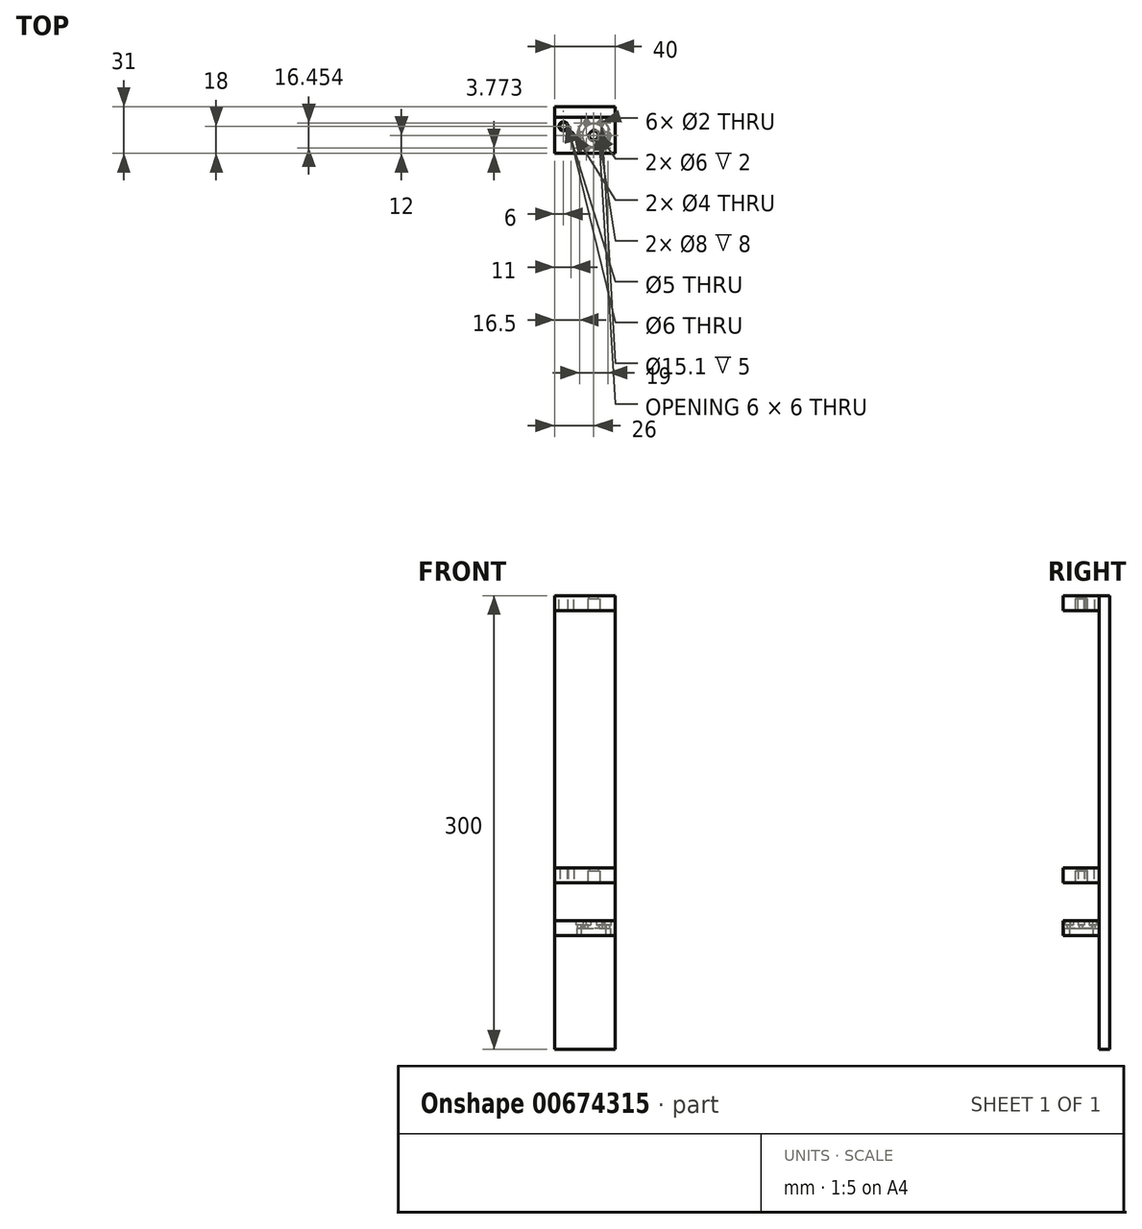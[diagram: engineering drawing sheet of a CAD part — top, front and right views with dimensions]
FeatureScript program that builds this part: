
annotation { "Feature Type Name" : "Feature", "Feature Type Description" : "" }
export const myFeature = defineFeature(function(context is Context, id is Id, definition is map)
    precondition{}
    {
        {
            var Q0;
            Q0=qCreatedBy(makeId("Top.planeOp"),FACE);
            var sketch = newSketch(context, id + "F0", { "sketchPlane" : qUnion([Q0])});
            skLineSegment(sketch, "E0.bottom", {"start": v(0, 0) * mm, "end": v(40, 0) * mm});
            skLineSegment(sketch, "E0.top", {"start": v(0, 24) * mm, "end": v(40, 24) * mm});
            skLineSegment(sketch, "E0.left", {"start": v(0, 0) * mm, "end": v(0, 24) * mm});
            skLineSegment(sketch, "E0.right", {"start": v(40, 0) * mm, "end": v(40, 24) * mm});
            skCircle(sketch, "E1", {"center": v(26, 12) * mm, "radius": 7.55 * mm});
            skLineSegment(sketch, "E2", {"start": v(0, 12) * mm, "end": v(40, 12) * mm, "construction": true});
            skSolve(sketch);
        }
        {
            var Q0;
            Q0 = qSketchRegion(id + "F0", true);
            extrude(context, id + "F1", {"entities" : qUnion([Q0]), "depth" : 10 * mm, "offsetDistance" : 25 * mm});
        }
        {
            var Q0;
            Q0=makeQuery(id+"F1.opExtrude","CAP_FACE",FACE,{"disambiguationData":[OSD([sQuery(id+"F0.wireOp",EDGE,"E0.bottom"),sQuery(id+"F0.wireOp",EDGE,"E0.top"),sQuery(id+"F0.wireOp",EDGE,"E0.left"),sQuery(id+"F0.wireOp",EDGE,"E0.right"),sQuery(id+"F0.wireOp",EDGE,"E1")])],"isStart":false});
            var sketch = newSketch(context, id + "F2", { "sketchPlane" : qUnion([Q0])});
            skCircle(sketch, "E3.cCircle", {"center": v(26, 12) * mm, "radius": 9.5 * mm, "construction": true});
            skLineSegment(sketch, "E3.0", {"start": v(21.25, 20.23) * mm, "end": v(30.75, 20.23) * mm, "construction": true});
            skLineSegment(sketch, "E3.1", {"start": v(30.75, 20.23) * mm, "end": v(35.5, 12) * mm, "construction": true});
            skLineSegment(sketch, "E3.2", {"start": v(35.5, 12) * mm, "end": v(30.75, 3.77) * mm, "construction": true});
            skLineSegment(sketch, "E3.3", {"start": v(30.75, 3.77) * mm, "end": v(21.25, 3.77) * mm, "construction": true});
            skLineSegment(sketch, "E3.4", {"start": v(21.25, 3.77) * mm, "end": v(16.5, 12) * mm, "construction": true});
            skLineSegment(sketch, "E3.5", {"start": v(16.5, 12) * mm, "end": v(21.25, 20.23) * mm, "construction": true});
            skLineSegment(sketch, "E4", {"start": v(21.25, 20.23) * mm, "end": v(30.75, 3.77) * mm, "construction": true});
            skPoint(sketch, "E5", {"position": v(21.25, 20.23) * mm});
            skPoint(sketch, "E6", {"position": v(16.5, 12) * mm});
            skPoint(sketch, "E7", {"position": v(21.25, 3.77) * mm});
            skPoint(sketch, "E8", {"position": v(30.75, 3.77) * mm});
            skPoint(sketch, "E9", {"position": v(35.5, 12) * mm});
            skPoint(sketch, "E10", {"position": v(30.75, 20.23) * mm});
            skSolve(sketch);
        }
        {
            var Q0;
            Q0=sQuery(id+"F2.wireOp",VERTEX,"E5");
            var Q1;
            Q1=sQuery(id+"F2.wireOp",VERTEX,"E6");
            var Q2;
            Q2=sQuery(id+"F2.wireOp",VERTEX,"E7");
            var Q3;
            Q3=sQuery(id+"F2.wireOp",VERTEX,"E8");
            var Q4;
            Q4=sQuery(id+"F2.wireOp",VERTEX,"E9");
            var Q5;
            Q5=sQuery(id+"F2.wireOp",VERTEX,"E10");
            var Q6;
            Q6=makeQuery(id+"F1.opExtrude","SWEPT_BODY",BODY,{"disambiguationData":[OSD([sQuery(id+"F0.wireOp",EDGE,"E0.bottom"),sQuery(id+"F0.wireOp",EDGE,"E0.top"),sQuery(id+"F0.wireOp",EDGE,"E0.left"),sQuery(id+"F0.wireOp",EDGE,"E0.right"),sQuery(id+"F0.wireOp",EDGE,"E1")])]});
            hole(context, id + "F3", {"style" : HoleStyle.SIMPLE, "endStyle" : HoleEndStyle.BLIND, "holeDiameter" : 2 * mm, "majorDiameter" : 5 * mm, "holeDepth" : 18 * mm, "isTappedThrough" : true, "tappedDepth" : 7 * mm, "tapClearance" : 2, "startFromSketch" : true, "locations" : qUnion([Q0, Q1, Q2, Q3, Q4, Q5]), "scope" : qUnion([Q6])});
        }
        {
            var Q0;
            Q0=makeQuery(id+"F1.opExtrude","CAP_FACE",FACE,{"disambiguationData":[OSD([sQuery(id+"F0.wireOp",EDGE,"E0.bottom"),sQuery(id+"F0.wireOp",EDGE,"E0.top"),sQuery(id+"F0.wireOp",EDGE,"E0.left"),sQuery(id+"F0.wireOp",EDGE,"E0.right"),sQuery(id+"F0.wireOp",EDGE,"E1")])],"isStart":false});
            var sketch = newSketch(context, id + "F4", { "sketchPlane" : qUnion([Q0])});
            skCircle(sketch, "E11", {"center": v(21.25, 20.23) * mm, "radius": 2 * mm});
            skCircle(sketch, "E12", {"center": v(30.75, 3.77) * mm, "radius": 2 * mm});
            skLineSegment(sketch, "E13", {"start": v(19.52, 19.23) * mm, "end": v(29.02, 2.77) * mm});
            skLineSegment(sketch, "E14", {"start": v(22.98, 21.23) * mm, "end": v(32.48, 4.77) * mm});
            skLineSegment(sketch, "E15.1.0", {"start": v(22.98, 2.77) * mm, "end": v(32.48, 19.23) * mm});
            skCircle(sketch, "E15.1.1", {"center": v(21.25, 3.77) * mm, "radius": 2 * mm});
            skLineSegment(sketch, "E15.1.2", {"start": v(19.52, 4.77) * mm, "end": v(29.02, 21.23) * mm});
            skCircle(sketch, "E15.1.3", {"center": v(30.75, 20.23) * mm, "radius": 2 * mm});
            skLineSegment(sketch, "E15.2.0", {"start": v(35.5, 14) * mm, "end": v(16.5, 14) * mm});
            skCircle(sketch, "E15.2.1", {"center": v(35.5, 12) * mm, "radius": 2 * mm});
            skLineSegment(sketch, "E15.2.2", {"start": v(35.5, 10) * mm, "end": v(16.5, 10) * mm});
            skCircle(sketch, "E15.2.3", {"center": v(16.5, 12) * mm, "radius": 2 * mm});
            skPoint(sketch, "E15.center", {"position": v(26, 12) * mm});
            skSolve(sketch);
        }
        {
            var Q0;
            Q0 = qSketchRegion(id + "F4", true);
            extrude(context, id + "F5", {"entities" : qUnion([Q0]), "operationType" : NewBodyOperationType.REMOVE, "oppositeDirection" : true, "depth" : 3 * mm, "offsetDistance" : 25 * mm});
        }
        {
            var Q0;
            Q0=makeQuery(id+"F1.opExtrude","CAP_FACE",FACE,{"disambiguationData":[OSD([sQuery(id+"F0.wireOp",EDGE,"E0.bottom"),sQuery(id+"F0.wireOp",EDGE,"E0.top"),sQuery(id+"F0.wireOp",EDGE,"E0.left"),sQuery(id+"F0.wireOp",EDGE,"E0.right"),sQuery(id+"F0.wireOp",EDGE,"E1")])],"isStart":true});
            var sketch = newSketch(context, id + "F6", { "sketchPlane" : qUnion([Q0])});
            skCircle(sketch, "E16", {"center": v(26, -12) * mm, "radius": 11.1 * mm});
            skLineSegment(sketch, "E17.bottom", {"start": v(18, -0.65) * mm, "end": v(34, -0.65) * mm});
            skLineSegment(sketch, "E17.top", {"start": v(18, -26.16) * mm, "end": v(34, -26.16) * mm});
            skLineSegment(sketch, "E17.left", {"start": v(18, -0.65) * mm, "end": v(18, -26.16) * mm});
            skLineSegment(sketch, "E17.right", {"start": v(34, -0.65) * mm, "end": v(34, -26.16) * mm});
            skLineSegment(sketch, "E18", {"start": v(26, -0.65) * mm, "end": v(26, -26.16) * mm, "construction": true});
            skSolve(sketch);
        }
        {
            var Q0;
            Q0 = qSketchRegion(id + "F6", true);
            extrude(context, id + "F7", {"entities" : qUnion([Q0]), "operationType" : NewBodyOperationType.REMOVE, "oppositeDirection" : true, "depth" : 5 * mm, "offsetDistance" : 25 * mm});
        }
        {
            var Q0;
            Q0=makeQuery(id+"F1.opExtrude","SWEPT_FACE",FACE,{"disambiguationData":[OSD([sQuery(id+"F0.wireOp",EDGE,"E0.top")])]});
            var sketch = newSketch(context, id + "F8", { "sketchPlane" : qUnion([Q0])});
            skLineSegment(sketch, "E19.bottom", {"start": v(0, 225) * mm, "end": v(-40, 225) * mm});
            skLineSegment(sketch, "E19.top", {"start": v(0, -75) * mm, "end": v(-40, -75) * mm});
            skLineSegment(sketch, "E19.left", {"start": v(0, 225) * mm, "end": v(0, -75) * mm});
            skLineSegment(sketch, "E19.right", {"start": v(-40, 225) * mm, "end": v(-40, -75) * mm});
            skSolve(sketch);
        }
        {
            var Q0;
            Q0 = qSketchRegion(id + "F8", true);
            extrude(context, id + "F9", {"entities" : qUnion([Q0]), "depth" : 7 * mm, "offsetDistance" : 25 * mm});
        }
        {
            var Q0;
            Q0=makeQuery(id+"F9.opExtrude","SWEPT_FACE",FACE,{"disambiguationData":[OSD([sQuery(id+"F8.wireOp",EDGE,"E19.bottom")])]});
            var sketch = newSketch(context, id + "F10", { "sketchPlane" : qUnion([Q0])});
            skLineSegment(sketch, "E20.bottom", {"start": v(0, 0) * mm, "end": v(40, 0) * mm});
            skLineSegment(sketch, "E20.top", {"start": v(0, 24) * mm, "end": v(40, 24) * mm});
            skLineSegment(sketch, "E20.left", {"start": v(0, 0) * mm, "end": v(0, 24) * mm});
            skLineSegment(sketch, "E20.right", {"start": v(40, 0) * mm, "end": v(40, 24) * mm});
            skCircle(sketch, "E21", {"center": v(26, 12) * mm, "radius": 3 * mm});
            skLineSegment(sketch, "E22", {"start": v(0, 12) * mm, "end": v(40, 12) * mm, "construction": true});
            skCircle(sketch, "E23", {"center": v(11, 12) * mm, "radius": 2 * mm});
            skCircle(sketch, "E24", {"center": v(6, 18) * mm, "radius": 3 * mm});
            skSolve(sketch);
        }
        {
            var Q0;
            Q0 = qSketchRegion(id + "F10", true);
            extrude(context, id + "F11", {"entities" : qUnion([Q0]), "oppositeDirection" : true, "depth" : 10 * mm, "offsetDistance" : 25 * mm});
        }
        {
            var Q0;
            Q0=makeQuery(id+"F11.opExtrude","CAP_FACE",FACE,{"disambiguationData":[OSD([sQuery(id+"F10.wireOp",EDGE,"E20.bottom"),sQuery(id+"F10.wireOp",EDGE,"E20.top"),sQuery(id+"F10.wireOp",EDGE,"E20.left"),sQuery(id+"F10.wireOp",EDGE,"E20.right"),sQuery(id+"F10.wireOp",EDGE,"E21"),sQuery(id+"F10.wireOp",EDGE,"E23")])],"isStart":false});
            var sketch = newSketch(context, id + "F12", { "sketchPlane" : qUnion([Q0])});
            skCircle(sketch, "E25", {"center": v(26, -12) * mm, "radius": 4 * mm});
            skSolve(sketch);
        }
        {
            var Q0;
            Q0 = qSketchRegion(id + "F12", true);
            extrude(context, id + "F13", {"entities" : qUnion([Q0]), "operationType" : NewBodyOperationType.REMOVE, "oppositeDirection" : true, "depth" : 8 * mm, "offsetDistance" : 25 * mm});
        }
        {
            var Q0;
            Q0=qCreatedBy(makeId("Top.planeOp"),FACE);
            cPlane(context, id + "F14", {"entities" : qUnion([Q0]), "cplaneType" : CPlaneType.OFFSET, "offset" : 35 * mm, "width" : 150 * mm, "height" : 150 * mm});
        }
        {
            var Q0;
            Q0=qCreatedBy(id+"F14.planeOp",FACE);
            var sketch = newSketch(context, id + "F15", { "sketchPlane" : qUnion([Q0])});
            skLineSegment(sketch, "E26.bottom", {"start": v(0, 0) * mm, "end": v(40, 0) * mm});
            skLineSegment(sketch, "E26.top", {"start": v(0, 24) * mm, "end": v(40, 24) * mm});
            skLineSegment(sketch, "E26.left", {"start": v(0, 0) * mm, "end": v(0, 24) * mm});
            skLineSegment(sketch, "E26.right", {"start": v(40, 0) * mm, "end": v(40, 24) * mm});
            skLineSegment(sketch, "E27", {"start": v(0, 12) * mm, "end": v(40, 12) * mm, "construction": true});
            skCircle(sketch, "E28", {"center": v(26, 12) * mm, "radius": 3 * mm});
            skCircle(sketch, "E29", {"center": v(11, 12) * mm, "radius": 2 * mm});
            skCircle(sketch, "E30", {"center": v(6, 18) * mm, "radius": 2.5 * mm});
            skSolve(sketch);
        }
        {
            var Q0;
            Q0 = qSketchRegion(id + "F15", true);
            extrude(context, id + "F16", {"entities" : qUnion([Q0]), "depth" : 10 * mm, "offsetDistance" : 25 * mm});
        }
        {
            var Q0;
            Q0=makeQuery(id+"F16.opExtrude","CAP_FACE",FACE,{"disambiguationData":[OSD([sQuery(id+"F15.wireOp",EDGE,"E26.bottom"),sQuery(id+"F15.wireOp",EDGE,"E26.top"),sQuery(id+"F15.wireOp",EDGE,"E26.left"),sQuery(id+"F15.wireOp",EDGE,"E26.right"),sQuery(id+"F15.wireOp",EDGE,"E28"),sQuery(id+"F15.wireOp",EDGE,"E29"),sQuery(id+"F15.wireOp",EDGE,"E30")])],"isStart":true});
            var sketch = newSketch(context, id + "F17", { "sketchPlane" : qUnion([Q0])});
            skCircle(sketch, "E31", {"center": v(26, -12) * mm, "radius": 4 * mm});
            skSolve(sketch);
        }
        {
            var Q0;
            Q0 = qSketchRegion(id + "F17", true);
            extrude(context, id + "F18", {"entities" : qUnion([Q0]), "operationType" : NewBodyOperationType.REMOVE, "oppositeDirection" : true, "depth" : 8 * mm, "offsetDistance" : 25 * mm});
        }
    });
